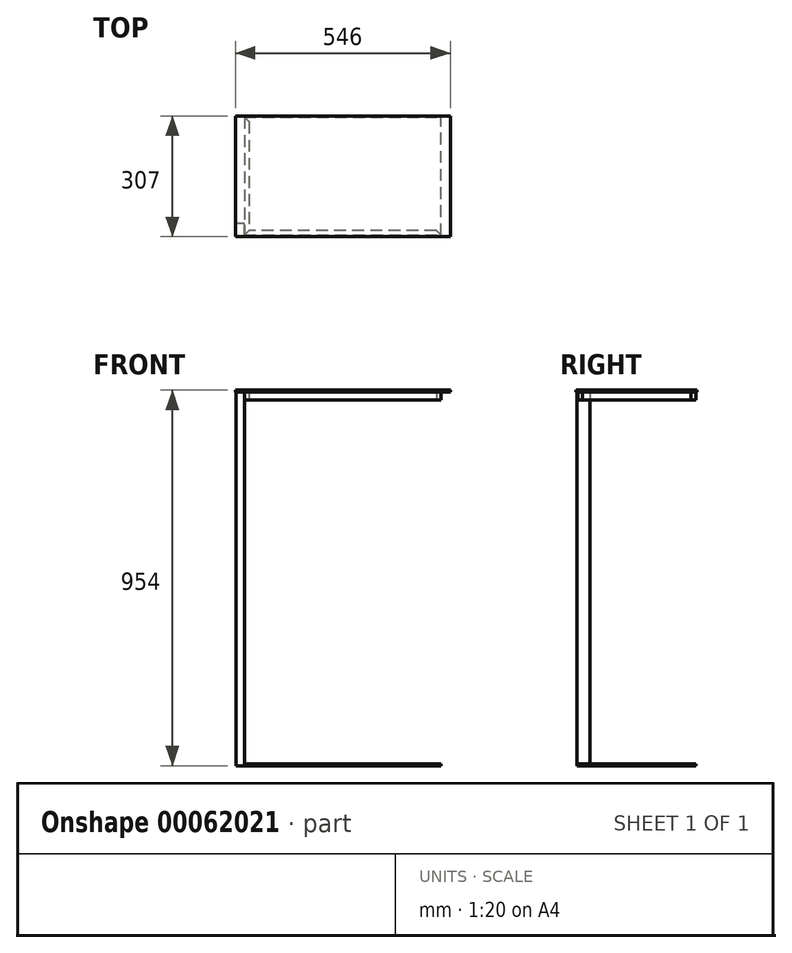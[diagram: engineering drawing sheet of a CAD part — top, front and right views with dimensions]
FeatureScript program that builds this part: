
annotation { "Feature Type Name" : "Feature", "Feature Type Description" : "" }
export const myFeature = defineFeature(function(context is Context, id is Id, definition is map)
    precondition{}
    {
        {
            var Q0;
            Q0=qCreatedBy(makeId("Top.planeOp"),FACE);
            var sketch = newSketch(context, id + "F0", { "sketchPlane" : qUnion([Q0])});
            skLineSegment(sketch, "E0.bottom", {"start": v(0, 0) * mm, "end": v(21, 0) * mm});
            skLineSegment(sketch, "E0.top", {"start": v(0, 33) * mm, "end": v(21, 33) * mm});
            skLineSegment(sketch, "E0.left", {"start": v(0, 0) * mm, "end": v(0, 33) * mm});
            skLineSegment(sketch, "E0.right", {"start": v(21, 0) * mm, "end": v(21, 33) * mm});
            skSolve(sketch);
        }
        {
            var Q0;
            Q0 = qSketchRegion(id + "F0", true);
            extrude(context, id + "F1", {"entities" : qUnion([Q0]), "depth" : 950 * mm});
        }
        {
            var Q0;
            Q0=makeQuery(id+"F1.opExtrude","SWEPT_FACE",FACE,{"disambiguationData":[OSD([sQuery(id+"F0.wireOp",EDGE,"E0.bottom")])]});
            cPlane(context, id + "F2", {"entities" : qUnion([Q0]), "cplaneType" : CPlaneType.OFFSET, "offset" : 2 * mm, "oppositeDirection" : true, "width" : 150 * mm, "height" : 150 * mm});
        }
        {
            var Q0;
            Q0=qCreatedBy(id+"F2.planeOp",FACE);
            var sketch = newSketch(context, id + "F3", { "sketchPlane" : qUnion([Q0])});
            skLineSegment(sketch, "E1", {"start": v(21, 950) * mm, "end": v(33, 950) * mm});
            skLineSegment(sketch, "E2", {"start": v(21, 929) * mm, "end": v(21, 950) * mm});
            skLineSegment(sketch, "E3", {"start": v(33, 950) * mm, "end": v(33, 929) * mm});
            skLineSegment(sketch, "E4", {"start": v(33, 929) * mm, "end": v(21, 929) * mm});
            skSolve(sketch);
        }
        {
            var Q0;
            Q0 = qSketchRegion(id + "F3", true);
            extrude(context, id + "F4", {"entities" : qUnion([Q0]), "oppositeDirection" : true, "depth" : 300 * mm});
        }
        {
            var Q0;
            Q0=makeQuery(id+"F4.opExtrude","CAP_EDGE",EDGE,{"disambiguationData":[OSD([sQuery(id+"F3.wireOp",EDGE,"E3")])],"isStart":true});
            var Q1;
            Q1=makeQuery(id+"F4.opExtrude","CAP_EDGE",EDGE,{"disambiguationData":[OSD([sQuery(id+"F3.wireOp",EDGE,"E3")])],"isStart":false});
            chamfer(context, id + "F5", {"entities" : qUnion([Q0, Q1]), "width" : 12 * mm, "tangentPropagation" : true});
        }
        {
            var Q0;
            Q0=makeQuery(id+"F1.opExtrude","SWEPT_FACE",FACE,{"disambiguationData":[OSD([sQuery(id+"F0.wireOp",EDGE,"E0.right")])]});
            var sketch = newSketch(context, id + "F6", { "sketchPlane" : qUnion([Q0])});
            skLineSegment(sketch, "E5.bottom", {"start": v(2, 950) * mm, "end": v(14, 950) * mm});
            skLineSegment(sketch, "E5.top", {"start": v(2, 929) * mm, "end": v(14, 929) * mm});
            skLineSegment(sketch, "E5.left", {"start": v(2, 950) * mm, "end": v(2, 929) * mm});
            skLineSegment(sketch, "E5.right", {"start": v(14, 950) * mm, "end": v(14, 929) * mm});
            skSolve(sketch);
        }
        {
            var Q0;
            Q0 = qSketchRegion(id + "F6", true);
            extrude(context, id + "F7", {"entities" : qUnion([Q0]), "depth" : 500 * mm});
        }
        {
            var Q0;
            Q0=makeQuery(id+"F7.opExtrude","CAP_EDGE",EDGE,{"disambiguationData":[OSD([sQuery(id+"F6.wireOp",EDGE,"E5.right")])],"isStart":true});
            var Q1;
            Q1=makeQuery(id+"F7.opExtrude","CAP_EDGE",EDGE,{"disambiguationData":[OSD([sQuery(id+"F6.wireOp",EDGE,"E5.right")])],"isStart":false});
            chamfer(context, id + "F8", {"entities" : qUnion([Q0, Q1]), "width" : 12 * mm, "tangentPropagation" : true});
        }
        {
            var Q0;
            Q0=makeQuery(id+"F1.opExtrude","CAP_FACE",FACE,{"disambiguationData":[OSD([sQuery(id+"F0.wireOp",EDGE,"E0.bottom"),sQuery(id+"F0.wireOp",EDGE,"E0.top"),sQuery(id+"F0.wireOp",EDGE,"E0.left"),sQuery(id+"F0.wireOp",EDGE,"E0.right")])],"isStart":false});
            var sketch = newSketch(context, id + "F9", { "sketchPlane" : qUnion([Q0])});
            skLineSegment(sketch, "E6.bottom", {"start": v(-2, -2) * mm, "end": v(544, -2) * mm});
            skLineSegment(sketch, "E6.top", {"start": v(-2, 305) * mm, "end": v(544, 305) * mm});
            skLineSegment(sketch, "E6.left", {"start": v(-2, -2) * mm, "end": v(-2, 305) * mm});
            skLineSegment(sketch, "E6.right", {"start": v(544, -2) * mm, "end": v(544, 305) * mm});
            skLineSegment(sketch, "E7.bottom", {"start": v(521, 33) * mm, "end": v(542, 33) * mm, "construction": true});
            skLineSegment(sketch, "E7.top", {"start": v(521, 0) * mm, "end": v(542, 0) * mm, "construction": true});
            skLineSegment(sketch, "E7.left", {"start": v(521, 33) * mm, "end": v(521, 0) * mm, "construction": true});
            skLineSegment(sketch, "E7.right", {"start": v(542, 33) * mm, "end": v(542, 0) * mm, "construction": true});
            skLineSegment(sketch, "E8.bottom", {"start": v(0, 304) * mm, "end": v(21, 304) * mm, "construction": true});
            skLineSegment(sketch, "E8.top", {"start": v(0, 271) * mm, "end": v(21, 271) * mm, "construction": true});
            skLineSegment(sketch, "E8.left", {"start": v(0, 304) * mm, "end": v(0, 271) * mm, "construction": true});
            skLineSegment(sketch, "E8.right", {"start": v(21, 304) * mm, "end": v(21, 271) * mm, "construction": true});
            skLineSegment(sketch, "E9", {"start": v(21, 0) * mm, "end": v(21, 2) * mm, "construction": true});
            skLineSegment(sketch, "E10", {"start": v(21, 304) * mm, "end": v(21, 302) * mm, "construction": true});
            skSolve(sketch);
        }
        {
            var Q0;
            Q0 = qSketchRegion(id + "F9", true);
            extrude(context, id + "F10", {"entities" : qUnion([Q0]), "depth" : 4 * mm});
        }
        {
            var Q0;
            Q0=qCreatedBy(makeId("Top.planeOp"),FACE);
            var sketch = newSketch(context, id + "F11", { "sketchPlane" : qUnion([Q0])});
            skLineSegment(sketch, "E11.bottom", {"start": v(21, 2) * mm, "end": v(521, 2) * mm});
            skLineSegment(sketch, "E11.top", {"start": v(21, 302) * mm, "end": v(521, 302) * mm});
            skLineSegment(sketch, "E11.left", {"start": v(21, 2) * mm, "end": v(21, 302) * mm});
            skLineSegment(sketch, "E11.right", {"start": v(521, 2) * mm, "end": v(521, 302) * mm});
            skSolve(sketch);
        }
        {
            var Q0;
            Q0 = qSketchRegion(id + "F11", true);
            extrude(context, id + "F12", {"entities" : qUnion([Q0]), "depth" : 4 * mm});
        }
    });
